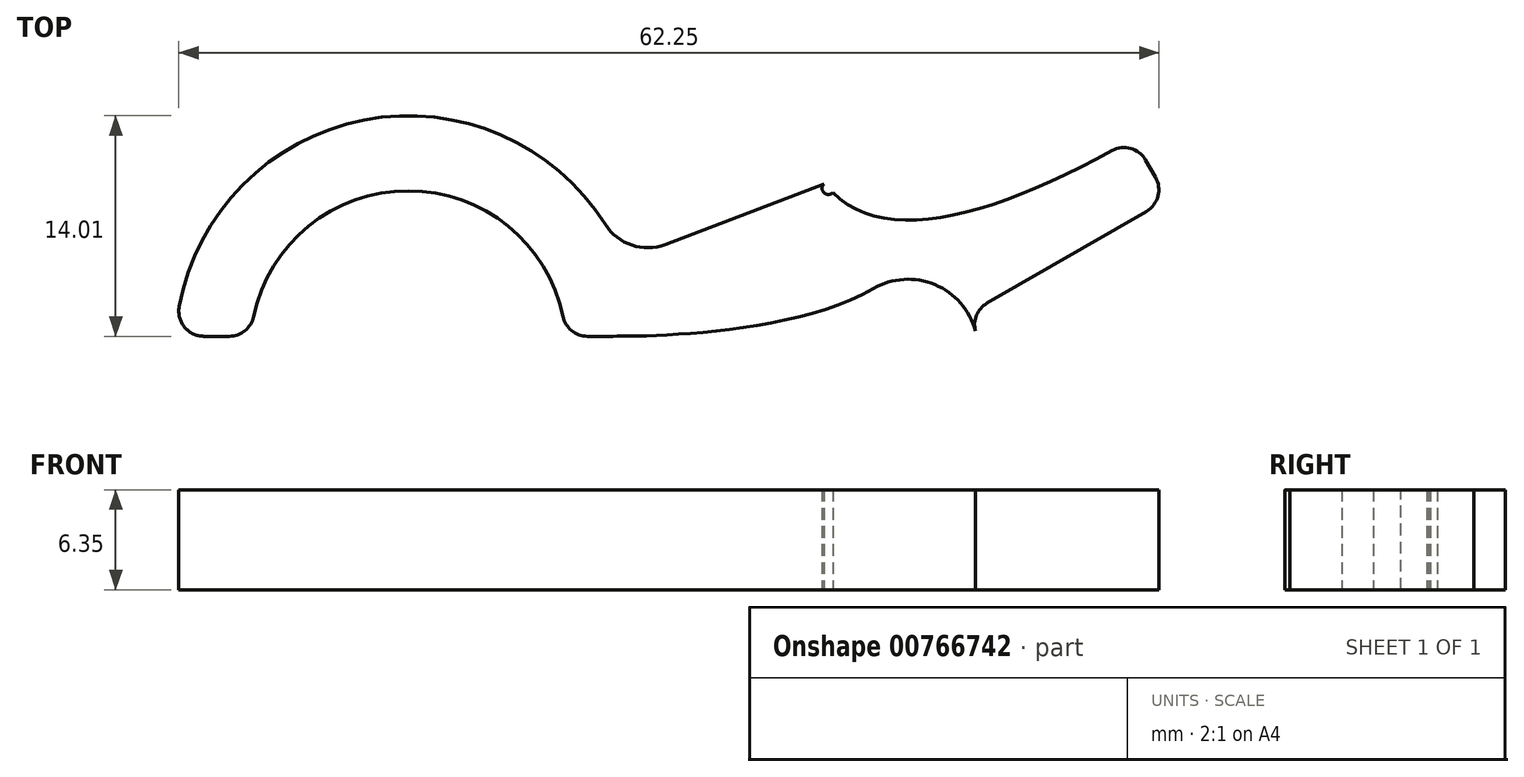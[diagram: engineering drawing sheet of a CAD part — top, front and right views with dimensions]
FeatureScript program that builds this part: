
annotation { "Feature Type Name" : "Feature", "Feature Type Description" : "" }
export const myFeature = defineFeature(function(context is Context, id is Id, definition is map)
    precondition{}
    {
        {
            var Q0;
            Q0=qCreatedBy(makeId("Top.planeOp"),FACE);
            var sketch = newSketch(context, id + "F0", { "sketchPlane" : qUnion([Q0])});
            skCircle(sketch, "E0", {"center": v(0, 0) * mm, "radius": 3.62 * mm, "construction": true});
            skLineSegment(sketch, "E1", {"start": v(2.56, 2.56) * mm, "end": v(-5.07, 10.2) * mm, "construction": true});
            skLineSegment(sketch, "E2", {"start": v(2.56, -2.56) * mm, "end": v(-5.07, -10.2) * mm, "construction": true});
            skCircle(sketch, "E3", {"center": v(-31.75, 0) * mm, "radius": 4.95 * mm, "construction": true});
            skCircle(sketch, "E4.0", {"center": v(-31.75, 0) * mm, "radius": 11.3 * mm, "construction": true});
            skLineSegment(sketch, "E5", {"start": v(0, 0) * mm, "end": v(-41.78, 0) * mm});
            skArc(sketch, "E6", {"start": v(-46.3, -2.67) * mm, "mid": v(-31.75, -14.8) * mm, "end": v(-17.2, -2.67) * mm});
            skArc(sketch, "E7", {"start": v(-19.24, 7.9) * mm, "mid": v(-34.56, 14.53) * mm, "end": v(-46.3, 2.67) * mm});
            skLineSegment(sketch, "E8", {"start": v(-41.78, 0) * mm, "end": v(-46.55, 0) * mm});
            skArc(sketch, "E9", {"start": v(-41.57, -2.06) * mm, "mid": v(-31.75, -10.03) * mm, "end": v(-21.93, -2.06) * mm});
            skArc(sketch, "E10", {"start": v(-21.93, 2.06) * mm, "mid": v(-31.75, 10.03) * mm, "end": v(-41.57, 2.06) * mm});
            skLineSegment(sketch, "E11", {"start": v(-44.74, 0.8) * mm, "end": v(-43.12, 0.8) * mm});
            skLineSegment(sketch, "E12", {"start": v(-43.12, -0.8) * mm, "end": v(-44.74, -0.8) * mm});
            skPoint(sketch, "E13.newPointB", {"position": v(-51.13, 0.8) * mm});
            skArc(sketch, "E13.filletArc", {"start": v(-46.3, 2.67) * mm, "mid": v(-45.96, 1.36) * mm, "end": v(-44.74, 0.8) * mm});
            skArc(sketch, "E14.filletArc", {"start": v(-43.12, 0.8) * mm, "mid": v(-42.12, 1.15) * mm, "end": v(-41.57, 2.06) * mm});
            skPoint(sketch, "E15.newPointB", {"position": v(-51.13, -0.8) * mm});
            skArc(sketch, "E15.filletArc", {"start": v(-44.74, -0.8) * mm, "mid": v(-45.96, -1.36) * mm, "end": v(-46.3, -2.67) * mm});
            skPoint(sketch, "E16.newPointA", {"position": v(-11.12, -0.8) * mm});
            skArc(sketch, "E16.filletArc", {"start": v(-41.57, -2.06) * mm, "mid": v(-42.12, -1.15) * mm, "end": v(-43.12, -0.8) * mm});
            skArc(sketch, "E17.0", {"start": v(4.41, 0) * mm, "mid": v(2.2, 3.82) * mm, "end": v(-2.2, 3.82) * mm});
            skCircle(sketch, "E18", {"center": v(-5.07, 10.2) * mm, "radius": 0.4 * mm});
            skCircle(sketch, "E19", {"center": v(-5.07, -10.2) * mm, "radius": 0.4 * mm});
            skLineSegment(sketch, "E20", {"start": v(-20.38, 0.8) * mm, "end": v(-18.76, 0.8) * mm});
            skLineSegment(sketch, "E21", {"start": v(-18.76, -0.8) * mm, "end": v(-20.38, -0.8) * mm});
            skPoint(sketch, "E22.visualSharp", {"position": v(-21.75, 0.8) * mm});
            skArc(sketch, "E22.filletArc", {"start": v(-21.93, 2.06) * mm, "mid": v(-21.38, 1.15) * mm, "end": v(-20.38, 0.8) * mm});
            skPoint(sketch, "E23.visualSharp", {"position": v(-16.98, 0.8) * mm});
            skPoint(sketch, "E24.visualSharp", {"position": v(-16.98, -0.8) * mm});
            skArc(sketch, "E24.filletArc", {"start": v(-17.2, -2.67) * mm, "mid": v(-17.54, -1.36) * mm, "end": v(-18.76, -0.8) * mm});
            skPoint(sketch, "E25.visualSharp", {"position": v(-21.75, -0.8) * mm});
            skArc(sketch, "E25.filletArc", {"start": v(-20.38, -0.8) * mm, "mid": v(-21.38, -1.15) * mm, "end": v(-21.93, -2.06) * mm});
            skLineSegment(sketch, "E26", {"start": v(-2.2, 3.82) * mm, "end": v(14.3, 13.35) * mm, "construction": true});
            skLineSegment(sketch, "E27", {"start": v(-5.07, 10.2) * mm, "end": v(-31.75, 0) * mm, "construction": true});
            skLineSegment(sketch, "E28", {"start": v(-5.07, -10.2) * mm, "end": v(-31.75, 0) * mm, "construction": true});
            skLineSegment(sketch, "E29", {"start": v(-15.42, 6.63) * mm, "end": v(-5.35, 10.47) * mm});
            skLineSegment(sketch, "E30", {"start": v(-17.93, -5.28) * mm, "end": v(-5.23, -10.56) * mm});
            skLineSegment(sketch, "E31", {"start": v(-5.07, 10.2) * mm, "end": v(-5.35, 9.91) * mm, "construction": true});
            skLineSegment(sketch, "E32", {"start": v(-5.07, 10.2) * mm, "end": v(-5.35, 10.47) * mm, "construction": true});
            skPoint(sketch, "E33", {"position": v(-4.8, 9.91) * mm});
            skFitSpline(sketch, "E34", {"points": [v(-4.8, 9.91) * mm, v(14.3, 13.35) * mm], "startDerivative": vector(10.6, -10.6) * mm, "endDerivative": vector(24.75, 14.29) * mm});
            skLineSegment(sketch, "E35", {"start": v(15.08, 11.99) * mm, "end": v(15.7, 10.9) * mm});
            skArc(sketch, "E36.filletArc", {"start": v(-19.24, 7.9) * mm, "mid": v(-17.56, 6.58) * mm, "end": v(-15.42, 6.63) * mm});
            skArc(sketch, "E37.filletArc", {"start": v(15.08, 11.99) * mm, "mid": v(14.13, 12.72) * mm, "end": v(12.94, 12.58) * mm});
            skLineSegment(sketch, "E38", {"start": v(0, 0) * mm, "end": v(42.6, 0) * mm, "construction": true});
            skPoint(sketch, "E39", {"position": v(4.41, 0) * mm});
            skFitSpline(sketch, "E40", {"points": [v(-18.76, 0.8) * mm, v(-2.2, 3.82) * mm], "startDerivative": vector(5.35, 0) * mm, "endDerivative": vector(15.74, 9.08) * mm});
            skLineSegment(sketch, "E41", {"start": v(-7.45, 0.8) * mm, "end": v(-2.2, 3.82) * mm, "construction": true});
            skLineSegment(sketch, "E42", {"start": v(0, 0) * mm, "end": v(21.52, 12.42) * mm, "construction": true});
            skLineSegment(sketch, "E43", {"start": v(15.12, 8.73) * mm, "end": v(5.01, 2.9) * mm});
            skPoint(sketch, "E44.visualSharp", {"position": v(16.5, 9.53) * mm});
            skArc(sketch, "E44.filletArc", {"start": v(15.12, 8.73) * mm, "mid": v(15.86, 9.7) * mm, "end": v(15.7, 10.9) * mm});
            skArc(sketch, "E45", {"start": v(5.01, 2.9) * mm, "mid": v(4.34, 2.13) * mm, "end": v(4.27, 1.12) * mm});
            skSolve(sketch);
        }
        {
            var Q0;
            Q0=makeQuery(id+"F0.imprint","IMPRINT",FACE,{"disambiguationData":[TD([[makeQuery(id+"F0.imprint","IMPRINT",EDGE,{"derivedFrom":sQuery(id+"F0.wireOp",EDGE,"E7")}),1.0]])]});
            extrude(context, id + "F1", {"entities" : qUnion([Q0]), "depth" : 6.35 * mm, "offsetDistance" : 25.4 * mm});
        }
    });
